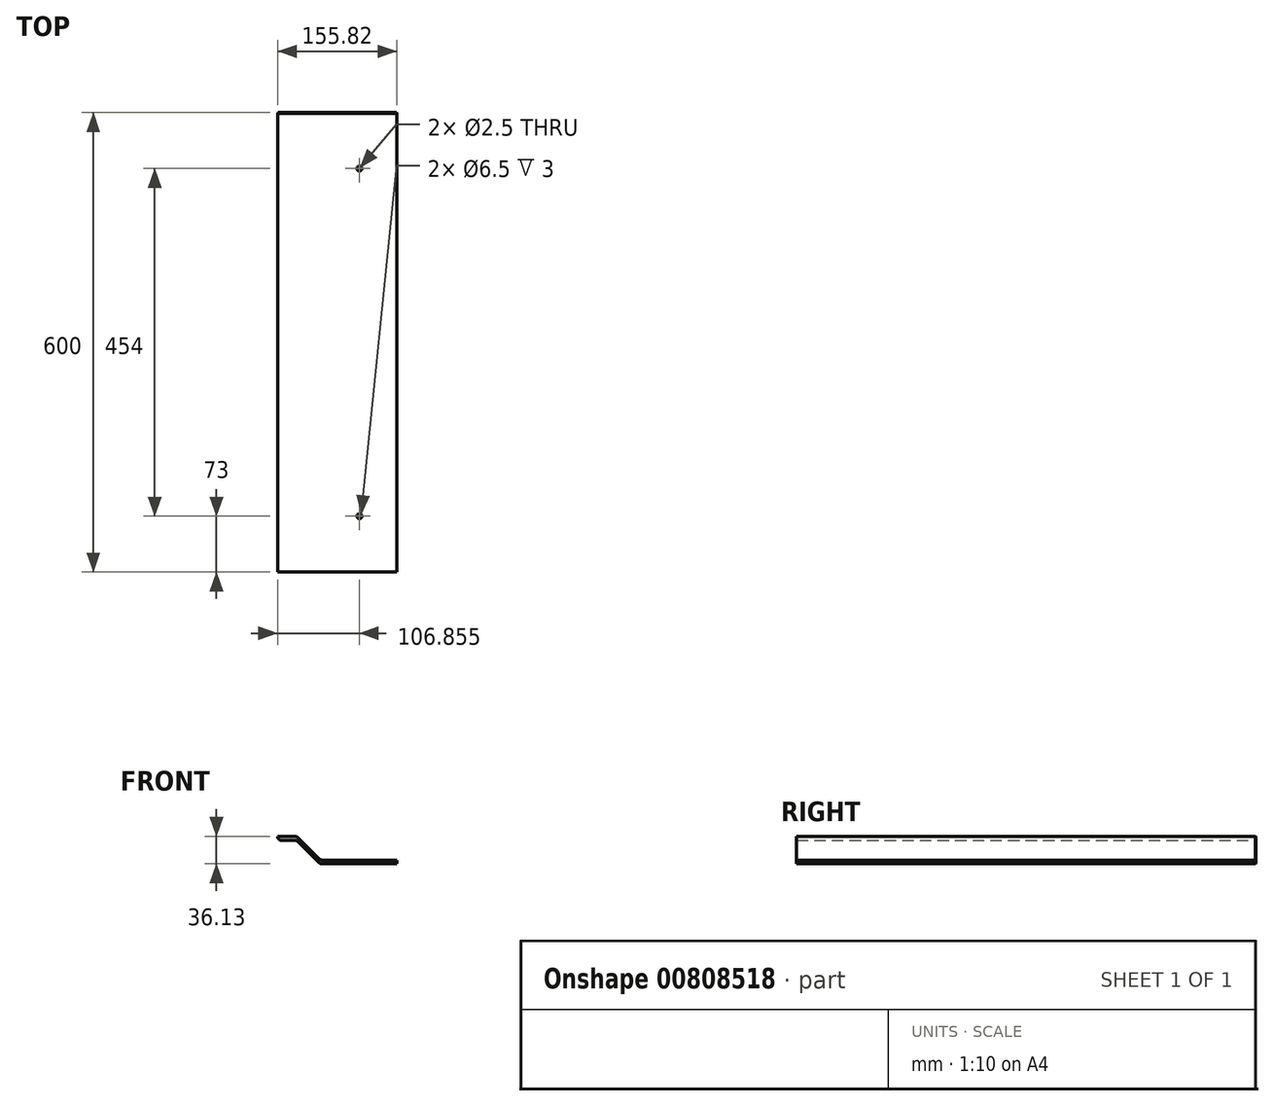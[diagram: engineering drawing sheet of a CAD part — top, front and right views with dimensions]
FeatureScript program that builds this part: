
annotation { "Feature Type Name" : "Feature", "Feature Type Description" : "" }
export const myFeature = defineFeature(function(context is Context, id is Id, definition is map)
    precondition{}
    {
        {
            var Q0;
            Q0=qCreatedBy(makeId("Front.planeOp"),FACE);
            var sketch = newSketch(context, id + "F0", { "sketchPlane" : qUnion([Q0])});
            skLineSegment(sketch, "E0", {"start": v(0, 12.61) * mm, "end": v(-100, 12.61) * mm});
            skLineSegment(sketch, "E1", {"start": v(-100, 12.61) * mm, "end": v(-130.64, 43.25) * mm});
            skLineSegment(sketch, "E2", {"start": v(-125.64, 43.25) * mm, "end": v(-100, 17.61) * mm});
            skLineSegment(sketch, "E3", {"start": v(-100, 17.61) * mm, "end": v(0, 17.61) * mm});
            skLineSegment(sketch, "E4", {"start": v(0, 17.61) * mm, "end": v(0, 12.61) * mm});
            skLineSegment(sketch, "E5", {"start": v(-130.64, 43.25) * mm, "end": v(-155.82, 43.25) * mm});
            skLineSegment(sketch, "E6", {"start": v(-155.82, 43.25) * mm, "end": v(-155.82, 48.8) * mm});
            skLineSegment(sketch, "E7", {"start": v(-125.64, 43.25) * mm, "end": v(-130.64, 48.25) * mm});
            skPoint(sketch, "E8.end.orphan", {"position": v(-125.64, 48.8) * mm});
            skLineSegment(sketch, "E9", {"start": v(-155.82, 48.8) * mm, "end": v(-130.64, 48.25) * mm});
            skLineSegment(sketch, "E10", {"start": v(73.18, 15.06) * mm, "end": v(-162.5, 15.06) * mm, "construction": true});
            skLineSegment(sketch, "E11.MirrorCS", {"start": v(0, 17.5) * mm, "end": v(-100, 17.5) * mm});
            skSolve(sketch);
        }
        {
            var Q0;
            Q0 = qSketchRegion(id + "F0", true);
            extrude(context, id + "F1", {"entities" : qUnion([Q0]), "depth" : 600 * mm, "offsetDistance" : 25 * mm});
        }
        {
            var Q0;
            Q0=makeQuery(id+"F1.opExtrude","SWEPT_EDGE",EDGE,{"disambiguationData":[OSD([sQuery(id+"F0.wireOp",EDGE,"E7"),sQuery(id+"F0.wireOp",EDGE,"E9")])]});
            var Q1;
            Q1=makeQuery(id+"F1.opExtrude","SWEPT_EDGE",EDGE,{"disambiguationData":[OSD([sQuery(id+"F0.wireOp",EDGE,"E2"),sQuery(id+"F0.wireOp",EDGE,"E3")])]});
            fillet(context, id + "F2", {"entities" : qUnion([Q0, Q1]), "radius" : 5 * mm, "tangentPropagation" : true, "allowEdgeOverflow" : false});
        }
        {
            var Q0;
            Q0=makeQuery(id+"F1.opExtrude","SWEPT_EDGE",EDGE,{"disambiguationData":[OSD([sQuery(id+"F0.wireOp",EDGE,"E1"),sQuery(id+"F0.wireOp",EDGE,"E5")])]});
            var Q1;
            Q1=makeQuery(id+"F1.opExtrude","SWEPT_EDGE",EDGE,{"disambiguationData":[OSD([sQuery(id+"F0.wireOp",EDGE,"E0"),sQuery(id+"F0.wireOp",EDGE,"E1")])]});
            var Q2;
            Q2=makeQuery(id+"F1.opExtrude","SWEPT_EDGE",EDGE,{"disambiguationData":[OSD([sQuery(id+"F0.wireOp",EDGE,"E5"),sQuery(id+"F0.wireOp",EDGE,"E6")])]});
            fillet(context, id + "F3", {"entities" : qUnion([Q0, Q1, Q2]), "radius" : 5 * mm, "tangentPropagation" : true, "allowEdgeOverflow" : false});
        }
        {
            var Q0;
            Q0=makeQuery(id+"F1.opExtrude","SWEPT_EDGE",EDGE,{"disambiguationData":[OSD([sQuery(id+"F0.wireOp",EDGE,"E6"),sQuery(id+"F0.wireOp",EDGE,"E9")])]});
            fillet(context, id + "F4", {"entities" : qUnion([Q0]), "radius" : 5 * mm, "tangentPropagation" : true, "allowEdgeOverflow" : false});
        }
        {
            var Q0;
            Q0=makeQuery(id+"F1.opExtrude","CAP_EDGE",EDGE,{"disambiguationData":[OSD([sQuery(id+"F0.wireOp",EDGE,"E3")])],"isStart":true});
            var Q1;
            Q1=makeQuery(id+"F1.opExtrude","CAP_EDGE",EDGE,{"disambiguationData":[OSD([sQuery(id+"F0.wireOp",EDGE,"E0")])],"isStart":true});
            var Q2;
            Q2=makeQuery(id+"F1.opExtrude","CAP_EDGE",EDGE,{"disambiguationData":[OSD([sQuery(id+"F0.wireOp",EDGE,"E1")])],"isStart":true});
            var Q3;
            {var subQ0=sQuery(id+"F0.wireOp",EDGE,"E5");var subQ1=sQuery(id+"F0.wireOp",EDGE,"E1");Q3=makeQuery(id+"F3.opFillet","BLEND_EDGE",EDGE,{"blendedFrom":[makeQuery(id+"F1.opExtrude","SWEPT_EDGE",EDGE,{"disambiguationData":[OSD([subQ1,subQ0])]}),makeQuery(id+"F1.opExtrude","CAP_FACE",FACE,{"disambiguationData":[OSD([sQuery(id+"F0.wireOp",EDGE,"E0"),subQ1,sQuery(id+"F0.wireOp",EDGE,"E2"),sQuery(id+"F0.wireOp",EDGE,"E3"),sQuery(id+"F0.wireOp",EDGE,"E4"),subQ0,sQuery(id+"F0.wireOp",EDGE,"E6"),sQuery(id+"F0.wireOp",EDGE,"E7"),sQuery(id+"F0.wireOp",EDGE,"E9")])],"isStart":true})],"blendedInto":[makeQuery(id+"F1.opExtrude","CAP_FACE",FACE,{"disambiguationData":[OSD([sQuery(id+"F0.wireOp",EDGE,"E0"),subQ1,sQuery(id+"F0.wireOp",EDGE,"E2"),sQuery(id+"F0.wireOp",EDGE,"E3"),sQuery(id+"F0.wireOp",EDGE,"E4"),subQ0,sQuery(id+"F0.wireOp",EDGE,"E6"),sQuery(id+"F0.wireOp",EDGE,"E7"),sQuery(id+"F0.wireOp",EDGE,"E9")])],"isStart":true})]});}
            var Q4;
            Q4=makeQuery(id+"F1.opExtrude","CAP_EDGE",EDGE,{"disambiguationData":[OSD([sQuery(id+"F0.wireOp",EDGE,"E5")])],"isStart":true});
            var Q5;
            {var subQ0=sQuery(id+"F0.wireOp",EDGE,"E6");var subQ1=sQuery(id+"F0.wireOp",EDGE,"E5");Q5=makeQuery(id+"F3.opFillet","BLEND_EDGE",EDGE,{"blendedFrom":[makeQuery(id+"F1.opExtrude","SWEPT_EDGE",EDGE,{"disambiguationData":[OSD([subQ1,subQ0])]}),makeQuery(id+"F1.opExtrude","CAP_FACE",FACE,{"disambiguationData":[OSD([sQuery(id+"F0.wireOp",EDGE,"E0"),sQuery(id+"F0.wireOp",EDGE,"E1"),sQuery(id+"F0.wireOp",EDGE,"E2"),sQuery(id+"F0.wireOp",EDGE,"E3"),sQuery(id+"F0.wireOp",EDGE,"E4"),subQ1,subQ0,sQuery(id+"F0.wireOp",EDGE,"E7"),sQuery(id+"F0.wireOp",EDGE,"E9")])],"isStart":true})],"blendedInto":[makeQuery(id+"F1.opExtrude","CAP_FACE",FACE,{"disambiguationData":[OSD([sQuery(id+"F0.wireOp",EDGE,"E0"),sQuery(id+"F0.wireOp",EDGE,"E1"),sQuery(id+"F0.wireOp",EDGE,"E2"),sQuery(id+"F0.wireOp",EDGE,"E3"),sQuery(id+"F0.wireOp",EDGE,"E4"),subQ1,subQ0,sQuery(id+"F0.wireOp",EDGE,"E7"),sQuery(id+"F0.wireOp",EDGE,"E9")])],"isStart":true})]});}
            var Q6;
            Q6=makeQuery(id+"F1.opExtrude","CAP_EDGE",EDGE,{"disambiguationData":[OSD([sQuery(id+"F0.wireOp",EDGE,"E9")])],"isStart":true});
            var Q7;
            {var subQ0=sQuery(id+"F0.wireOp",EDGE,"E9");var subQ1=sQuery(id+"F0.wireOp",EDGE,"E7");Q7=makeQuery(id+"F2.opFillet","BLEND_EDGE",EDGE,{"blendedFrom":[makeQuery(id+"F1.opExtrude","SWEPT_EDGE",EDGE,{"disambiguationData":[OSD([subQ1,subQ0])]}),makeQuery(id+"F1.opExtrude","CAP_FACE",FACE,{"disambiguationData":[OSD([sQuery(id+"F0.wireOp",EDGE,"E0"),sQuery(id+"F0.wireOp",EDGE,"E1"),sQuery(id+"F0.wireOp",EDGE,"E2"),sQuery(id+"F0.wireOp",EDGE,"E3"),sQuery(id+"F0.wireOp",EDGE,"E4"),sQuery(id+"F0.wireOp",EDGE,"E5"),sQuery(id+"F0.wireOp",EDGE,"E6"),subQ1,subQ0])],"isStart":true})],"blendedInto":[makeQuery(id+"F1.opExtrude","CAP_FACE",FACE,{"disambiguationData":[OSD([sQuery(id+"F0.wireOp",EDGE,"E0"),sQuery(id+"F0.wireOp",EDGE,"E1"),sQuery(id+"F0.wireOp",EDGE,"E2"),sQuery(id+"F0.wireOp",EDGE,"E3"),sQuery(id+"F0.wireOp",EDGE,"E4"),sQuery(id+"F0.wireOp",EDGE,"E5"),sQuery(id+"F0.wireOp",EDGE,"E6"),subQ1,subQ0])],"isStart":true})]});}
            var Q8;
            {var subQ0=sQuery(id+"F0.wireOp",EDGE,"E9");var subQ1=sQuery(id+"F0.wireOp",EDGE,"E6");Q8=makeQuery(id+"F4.opFillet","BLEND_EDGE",EDGE,{"blendedFrom":[makeQuery(id+"F1.opExtrude","SWEPT_EDGE",EDGE,{"disambiguationData":[OSD([subQ1,subQ0])]}),makeQuery(id+"F1.opExtrude","CAP_FACE",FACE,{"disambiguationData":[OSD([sQuery(id+"F0.wireOp",EDGE,"E0"),sQuery(id+"F0.wireOp",EDGE,"E1"),sQuery(id+"F0.wireOp",EDGE,"E2"),sQuery(id+"F0.wireOp",EDGE,"E3"),sQuery(id+"F0.wireOp",EDGE,"E4"),sQuery(id+"F0.wireOp",EDGE,"E5"),subQ1,sQuery(id+"F0.wireOp",EDGE,"E7"),subQ0])],"isStart":true})],"blendedInto":[makeQuery(id+"F1.opExtrude","CAP_FACE",FACE,{"disambiguationData":[OSD([sQuery(id+"F0.wireOp",EDGE,"E0"),sQuery(id+"F0.wireOp",EDGE,"E1"),sQuery(id+"F0.wireOp",EDGE,"E2"),sQuery(id+"F0.wireOp",EDGE,"E3"),sQuery(id+"F0.wireOp",EDGE,"E4"),sQuery(id+"F0.wireOp",EDGE,"E5"),subQ1,sQuery(id+"F0.wireOp",EDGE,"E7"),subQ0])],"isStart":true})]});}
            var Q9;
            {var subQ0=sQuery(id+"F0.wireOp",EDGE,"E1");var subQ1=sQuery(id+"F0.wireOp",EDGE,"E0");Q9=makeQuery(id+"F3.opFillet","BLEND_EDGE",EDGE,{"blendedFrom":[makeQuery(id+"F1.opExtrude","SWEPT_EDGE",EDGE,{"disambiguationData":[OSD([subQ1,subQ0])]}),makeQuery(id+"F1.opExtrude","CAP_FACE",FACE,{"disambiguationData":[OSD([subQ1,subQ0,sQuery(id+"F0.wireOp",EDGE,"E2"),sQuery(id+"F0.wireOp",EDGE,"E3"),sQuery(id+"F0.wireOp",EDGE,"E4"),sQuery(id+"F0.wireOp",EDGE,"E5"),sQuery(id+"F0.wireOp",EDGE,"E6"),sQuery(id+"F0.wireOp",EDGE,"E7"),sQuery(id+"F0.wireOp",EDGE,"E9")])],"isStart":true})],"blendedInto":[makeQuery(id+"F1.opExtrude","CAP_FACE",FACE,{"disambiguationData":[OSD([subQ1,subQ0,sQuery(id+"F0.wireOp",EDGE,"E2"),sQuery(id+"F0.wireOp",EDGE,"E3"),sQuery(id+"F0.wireOp",EDGE,"E4"),sQuery(id+"F0.wireOp",EDGE,"E5"),sQuery(id+"F0.wireOp",EDGE,"E6"),sQuery(id+"F0.wireOp",EDGE,"E7"),sQuery(id+"F0.wireOp",EDGE,"E9")])],"isStart":true})]});}
            var Q10;
            {var subQ0=sQuery(id+"F0.wireOp",EDGE,"E3");var subQ1=sQuery(id+"F0.wireOp",EDGE,"E2");Q10=makeQuery(id+"F2.opFillet","BLEND_EDGE",EDGE,{"blendedFrom":[makeQuery(id+"F1.opExtrude","SWEPT_EDGE",EDGE,{"disambiguationData":[OSD([subQ1,subQ0])]}),makeQuery(id+"F1.opExtrude","CAP_FACE",FACE,{"disambiguationData":[OSD([sQuery(id+"F0.wireOp",EDGE,"E0"),sQuery(id+"F0.wireOp",EDGE,"E1"),subQ1,subQ0,sQuery(id+"F0.wireOp",EDGE,"E4"),sQuery(id+"F0.wireOp",EDGE,"E5"),sQuery(id+"F0.wireOp",EDGE,"E6"),sQuery(id+"F0.wireOp",EDGE,"E7"),sQuery(id+"F0.wireOp",EDGE,"E9")])],"isStart":true})],"blendedInto":[makeQuery(id+"F1.opExtrude","CAP_FACE",FACE,{"disambiguationData":[OSD([sQuery(id+"F0.wireOp",EDGE,"E0"),sQuery(id+"F0.wireOp",EDGE,"E1"),subQ1,subQ0,sQuery(id+"F0.wireOp",EDGE,"E4"),sQuery(id+"F0.wireOp",EDGE,"E5"),sQuery(id+"F0.wireOp",EDGE,"E6"),sQuery(id+"F0.wireOp",EDGE,"E7"),sQuery(id+"F0.wireOp",EDGE,"E9")])],"isStart":true})]});}
            var Q11;
            Q11=makeQuery(id+"F1.opExtrude","CAP_EDGE",EDGE,{"disambiguationData":[OSD([sQuery(id+"F0.wireOp",EDGE,"E2"),sQuery(id+"F0.wireOp",EDGE,"E7")])],"isStart":true});
            var Q12;
            Q12=makeQuery(id+"F1.opExtrude","CAP_EDGE",EDGE,{"disambiguationData":[OSD([sQuery(id+"F0.wireOp",EDGE,"E4")])],"isStart":true});
            chamfer(context, id + "F5", {"entities" : qUnion([Q0, Q1, Q2, Q3, Q4, Q5, Q6, Q7, Q8, Q9, Q10, Q11, Q12]), "width" : 1 * mm, "tangentPropagation" : true});
        }
        {
            var Q0;
            Q0=makeQuery(id+"F1.opExtrude","SWEPT_FACE",FACE,{"disambiguationData":[OSD([sQuery(id+"F0.wireOp",EDGE,"E3")])]});
            var sketch = newSketch(context, id + "F6", { "sketchPlane" : qUnion([Q0])});
            skLineSegment(sketch, "E12", {"start": v(-48.96, -1) * mm, "end": v(-48.96, -600) * mm, "construction": true});
            skLineSegment(sketch, "E13", {"start": v(-97.93, -300.5) * mm, "end": v(0, -300.5) * mm, "construction": true});
            skLineSegment(sketch, "E14.MirrorCS", {"start": v(0, -300.5) * mm, "end": v(-97.93, -300.5) * mm, "construction": true});
            skPoint(sketch, "E15", {"position": v(-48.96, -73) * mm});
            skPoint(sketch, "E16", {"position": v(-48.96, -527) * mm});
            skSolve(sketch);
        }
        {
            var Q0;
            Q0=sQuery(id+"F6.wireOp",VERTEX,"E15");
            var Q1;
            Q1=sQuery(id+"F6.wireOp",VERTEX,"E16");
            var Q2;
            Q2=makeQuery(id+"F1.opExtrude","SWEPT_BODY",BODY,{"disambiguationData":[OSD([sQuery(id+"F0.wireOp",EDGE,"E1"),sQuery(id+"F0.wireOp",EDGE,"E2"),sQuery(id+"F0.wireOp",EDGE,"E3"),sQuery(id+"F0.wireOp",EDGE,"E4"),sQuery(id+"F0.wireOp",EDGE,"E5"),sQuery(id+"F0.wireOp",EDGE,"E6"),sQuery(id+"F0.wireOp",EDGE,"E7"),sQuery(id+"F0.wireOp",EDGE,"E9"),sQuery(id+"F0.wireOp",EDGE,"E0")])]});
            hole(context, id + "F7", {"style" : HoleStyle.C_BORE, "endStyle" : HoleEndStyle.THROUGH, "standardTappedOrClearance" : lookupTablePath({ "standard" : "ISO", "engagement" : "75%", "pitch" : "0.5 mm", "size" : "M3", "type" : "Tapped" }), "standardBlindInLast" : lookupTablePath({ "standard" : "ISO", "engagement" : "75%", "pitch" : "0.5 mm", "size" : "M3", "type" : "Tapped" }), "holeDiameter" : 2.5 * mm, "cBoreDiameter" : 6.5 * mm, "cBoreDepth" : 3 * mm, "majorDiameter" : 3 * mm, "showTappedDepth" : true, "isTappedThrough" : true, "tappedDepth" : 12 * mm, "tapClearance" : 3, "locations" : qUnion([Q0, Q1]), "scope" : qUnion([Q2])});
        }
    });
